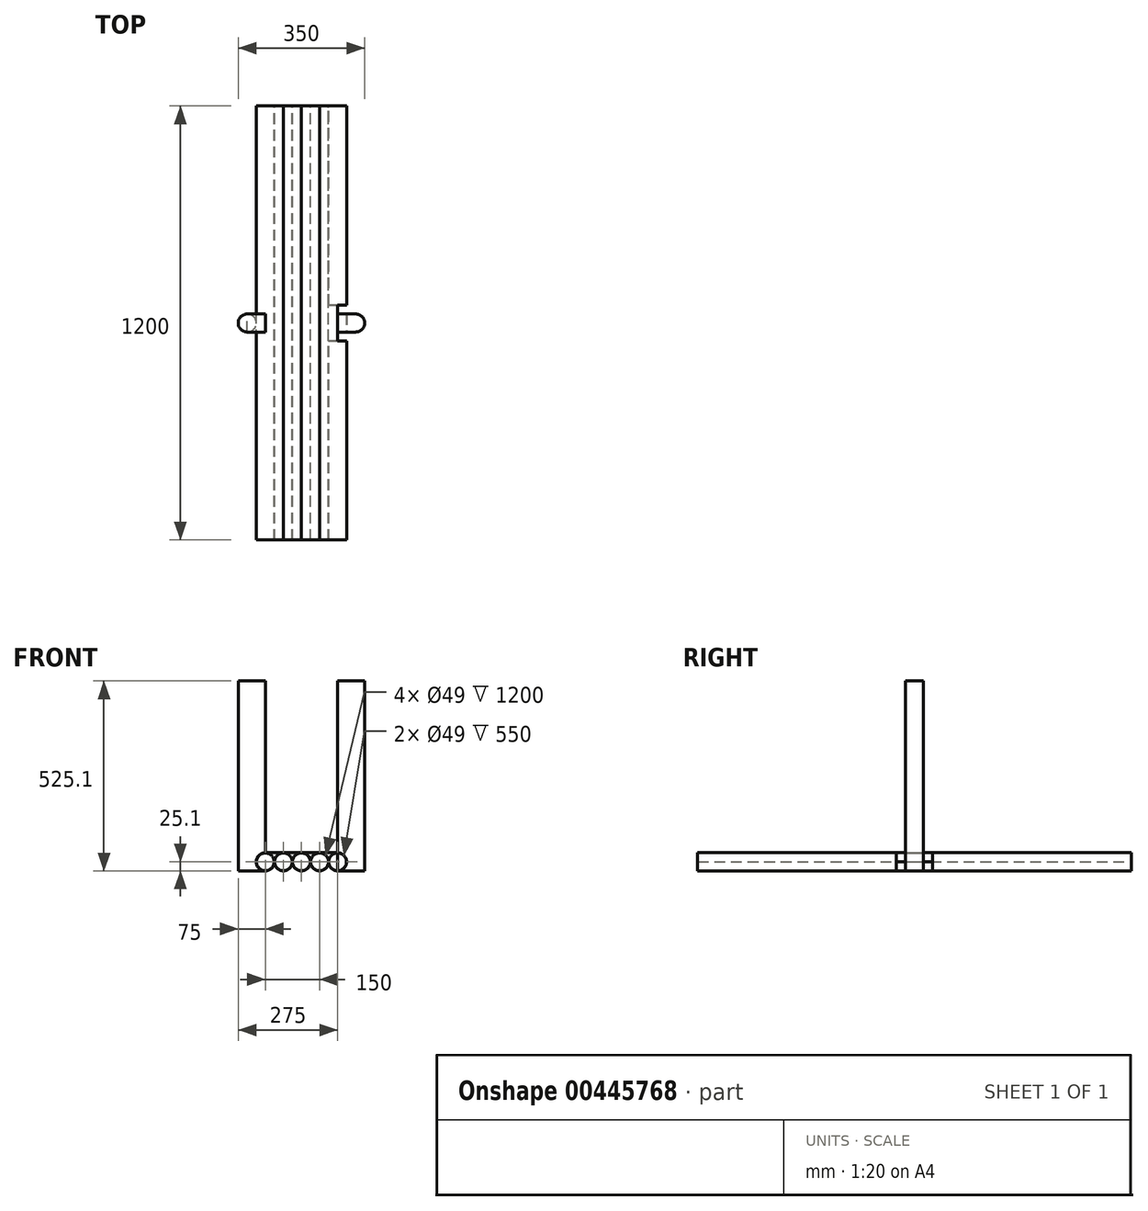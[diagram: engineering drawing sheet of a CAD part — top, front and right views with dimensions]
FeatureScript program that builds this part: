
annotation { "Feature Type Name" : "Feature", "Feature Type Description" : "" }
export const myFeature = defineFeature(function(context is Context, id is Id, definition is map)
    precondition{}
    {
        {
            var Q0;
            Q0=qCreatedBy(makeId("Front.planeOp"),FACE);
            var sketch = newSketch(context, id + "F0", { "sketchPlane" : qUnion([Q0])});
            skCircle(sketch, "E0", {"center": v(0, 0) * mm, "radius": 25 * mm});
            skCircle(sketch, "E1", {"center": v(0, 0) * mm, "radius": 24.5 * mm});
            skCircle(sketch, "E2", {"center": v(-50, 0) * mm, "radius": 25 * mm});
            skCircle(sketch, "E3.MirrorC", {"center": v(-50, 0) * mm, "radius": 24.5 * mm});
            skCircle(sketch, "E4.MirrorC", {"center": v(50, 0) * mm, "radius": 25 * mm});
            skCircle(sketch, "E5.MirrorC", {"center": v(50, 0) * mm, "radius": 24.5 * mm});
            skCircle(sketch, "E6.MirrorC", {"center": v(100, 0) * mm, "radius": 25 * mm});
            skCircle(sketch, "E7.MirrorC", {"center": v(100, 0) * mm, "radius": 24.5 * mm});
            skCircle(sketch, "E8.MirrorC", {"center": v(-100, 0) * mm, "radius": 25 * mm});
            skCircle(sketch, "E9.MirrorC", {"center": v(-100, 0) * mm, "radius": 24.5 * mm});
            skSolve(sketch);
        }
        {
            var Q0;
            Q0=qCreatedBy(makeId("Front.planeOp"),FACE);
            var sketch = newSketch(context, id + "F1", { "sketchPlane" : qUnion([Q0])});
            skCircle(sketch, "E10.0", {"center": v(-100, 0) * mm, "radius": 25 * mm});
            skCircle(sketch, "E11.0", {"center": v(-50, 0) * mm, "radius": 25 * mm});
            skCircle(sketch, "E12.0", {"center": v(0, 0) * mm, "radius": 24.5 * mm});
            skCircle(sketch, "E13.0", {"center": v(50, 0) * mm, "radius": 25 * mm});
            skCircle(sketch, "E14.0", {"center": v(100, 0) * mm, "radius": 25 * mm});
            skCircle(sketch, "E15.0", {"center": v(0, 0) * mm, "radius": 25 * mm});
            skLineSegment(sketch, "E16", {"start": v(-100, 0) * mm, "end": v(-100, 47.4) * mm, "construction": true});
            skLineSegment(sketch, "E17", {"start": v(-100, 25) * mm, "end": v(100, 25) * mm});
            skSolve(sketch);
        }
        {
            var Q0;
            Q0 = qSketchRegion(id + "F0", true);
            extrude(context, id + "F2", {"entities" : qUnion([Q0]), "endBound" : BoundingType.SYMMETRIC, "depth" : 1200 * mm});
        }
        {
            var Q0;
            {var subQ0=sQuery(id+"F1.wireOp",EDGE,"E17");var subQ1=sQuery(id+"F1.wireOp",EDGE,"E13.0");var subQ2=makeQuery(id+"F1.imprint","INTERSECT",VERTEX,{"derivedFrom":[subQ1,subQ0]});Q0=makeQuery(id+"F1.imprint","IMPRINT",FACE,{"disambiguationData":[TD([[makeQuery(id+"F1.imprint","IMPRINT",EDGE,{"disambiguationData":[TD([[subQ2,1.0]])],"derivedFrom":subQ1}),-1.0]])]});}
            var Q1;
            {var subQ0=sQuery(id+"F1.wireOp",EDGE,"E17");var subQ1=sQuery(id+"F1.wireOp",EDGE,"E13.0");var subQ2=makeQuery(id+"F1.imprint","INTERSECT",VERTEX,{"derivedFrom":[subQ1,subQ0]});Q1=makeQuery(id+"F1.imprint","IMPRINT",FACE,{"disambiguationData":[TD([[makeQuery(id+"F1.imprint","IMPRINT",EDGE,{"disambiguationData":[TD([[subQ2,-1.0]])],"derivedFrom":subQ1}),-1.0]])]});}
            var Q2;
            {var subQ0=sQuery(id+"F1.wireOp",EDGE,"E17");var subQ1=sQuery(id+"F1.wireOp",EDGE,"E11.0");var subQ2=makeQuery(id+"F1.imprint","INTERSECT",VERTEX,{"derivedFrom":[subQ1,subQ0]});Q2=makeQuery(id+"F1.imprint","IMPRINT",FACE,{"disambiguationData":[TD([[makeQuery(id+"F1.imprint","IMPRINT",EDGE,{"disambiguationData":[TD([[subQ2,1.0]])],"derivedFrom":subQ1}),-1.0]])]});}
            var Q3;
            {var subQ0=sQuery(id+"F1.wireOp",EDGE,"E17");var subQ1=sQuery(id+"F1.wireOp",EDGE,"E10.0");var subQ2=makeQuery(id+"F1.imprint","INTERSECT",VERTEX,{"derivedFrom":[subQ1,subQ0]});Q3=makeQuery(id+"F1.imprint","IMPRINT",FACE,{"disambiguationData":[TD([[makeQuery(id+"F1.imprint","IMPRINT",EDGE,{"disambiguationData":[TD([[subQ2,1.0]])],"derivedFrom":subQ1}),-1.0]])]});}
            extrude(context, id + "F3", {"entities" : qUnion([Q0, Q1, Q2, Q3]), "endBound" : BoundingType.SYMMETRIC, "depth" : 1200 * mm});
        }
        {
            var Q0;
            Q0=qCreatedBy(makeId("Top.planeOp"),FACE);
            var sketch = newSketch(context, id + "F4", { "sketchPlane" : qUnion([Q0])});
            skCircle(sketch, "E18", {"center": v(-150, 0) * mm, "radius": 25 * mm});
            skLineSegment(sketch, "E19", {"start": v(-75, -600) * mm, "end": v(-75, 600) * mm, "construction": true});
            skLineSegment(sketch, "E20", {"start": v(-150, 0) * mm, "end": v(-150, 25) * mm});
            skLineSegment(sketch, "E21", {"start": v(-150, 25) * mm, "end": v(-150, -25) * mm});
            skLineSegment(sketch, "E22.bottom", {"start": v(-150, -25) * mm, "end": v(-100, -25) * mm});
            skLineSegment(sketch, "E22.top", {"start": v(-150, 25) * mm, "end": v(-100, 25) * mm});
            skLineSegment(sketch, "E22.left", {"start": v(-150, -25) * mm, "end": v(-150, 25) * mm, "construction": true});
            skLineSegment(sketch, "E22.right", {"start": v(-100, -25) * mm, "end": v(-100, 25) * mm});
            skLineSegment(sketch, "E23.MirrorCS", {"start": v(150, -25) * mm, "end": v(100, -25) * mm});
            skLineSegment(sketch, "E24.MirrorCS", {"start": v(150, 25) * mm, "end": v(100, 25) * mm});
            skCircle(sketch, "E25.MirrorC", {"center": v(150, 0) * mm, "radius": 25 * mm});
            skLineSegment(sketch, "E26.MirrorCS", {"start": v(150, -25) * mm, "end": v(150, 25) * mm, "construction": true});
            skLineSegment(sketch, "E27.MirrorCS", {"start": v(100, -25) * mm, "end": v(100, 25) * mm});
            skLineSegment(sketch, "E28.bottom", {"start": v(-150, 25) * mm, "end": v(-125, 25) * mm});
            skLineSegment(sketch, "E28.top", {"start": v(-150, -25) * mm, "end": v(-125, -25) * mm});
            skLineSegment(sketch, "E28.right", {"start": v(-125, 25) * mm, "end": v(-125, -25) * mm});
            skSolve(sketch);
        }
        {
            var Q0;
            Q0 = qSketchRegion(id + "F4", true);
            extrude(context, id + "F5", {"entities" : qUnion([Q0]), "oppositeDirection" : true, "depth" : 25 * mm});
        }
        {
            var Q0;
            Q0 = qSketchRegion(id + "F4", true);
            extrude(context, id + "F6", {"entities" : qUnion([Q0]), "operationType" : NewBodyOperationType.ADD, "depth" : 500 * mm});
        }
        {
            var Q0;
            Q0=makeQuery(id+"F0.imprint","IMPRINT",FACE,{"disambiguationData":[TD([[makeQuery(id+"F0.imprint","IMPRINT",EDGE,{"derivedFrom":sQuery(id+"F0.wireOp",EDGE,"E9.MirrorC")}),1.0]])]});
            extrude(context, id + "F7", {"entities" : qUnion([Q0]), "operationType" : NewBodyOperationType.REMOVE, "endBound" : BoundingType.SYMMETRIC, "oppositeDirection" : true, "depth" : 100 * mm});
        }
        {
            var Q0;
            Q0=makeQuery(id+"F0.imprint","IMPRINT",FACE,{"disambiguationData":[TD([[makeQuery(id+"F0.imprint","IMPRINT",EDGE,{"derivedFrom":sQuery(id+"F0.wireOp",EDGE,"E7.MirrorC")}),-1.0]])]});
            extrude(context, id + "F8", {"entities" : qUnion([Q0]), "operationType" : NewBodyOperationType.REMOVE, "endBound" : BoundingType.SYMMETRIC, "oppositeDirection" : true, "depth" : 100 * mm});
        }
        {
            var Q0;
            {var subQ0=sQuery(id+"F4.wireOp",EDGE,"E22.bottom");Q0=makeQuery(id+"F6.boolean.opBoolean","MERGE",FACE,{"derivedFrom":[makeQuery(id+"F5.opExtrude","SWEPT_FACE",FACE,{"disambiguationData":[OSD([subQ0])]}),makeQuery(id+"F6.opExtrude","SWEPT_FACE",FACE,{"disambiguationData":[OSD([subQ0])]})]});}
            var sketch = newSketch(context, id + "F9", { "sketchPlane" : qUnion([Q0])});
            skCircle(sketch, "E29", {"center": v(-125, 475) * mm, "radius": 25 * mm});
            skSolve(sketch);
        }
        {
            var Q0;
            {var subQ0=sQuery(id+"F9.wireOp",EDGE,"E29");var subQ1=sQuery(id+"F4.wireOp",EDGE,"E22.bottom");var subQ2=makeQuery(id+"F9.imprint","INTERSECT",VERTEX,{"derivedFrom":[makeQuery(id+"F6.opExtrude","CAP_EDGE",EDGE,{"disambiguationData":[OSD([subQ1])],"isStart":false}),subQ0]});Q0=makeQuery(id+"F9.imprint","IMPRINT",FACE,{"disambiguationData":[TD([[makeQuery(id+"F9.imprint","IMPRINT",EDGE,{"disambiguationData":[TD([[subQ2,-1.0]])],"derivedFrom":subQ0}),1.0]])]});}
            extrude(context, id + "F10", {"entities" : qUnion([Q0]), "operationType" : NewBodyOperationType.ADD, "oppositeDirection" : true, "depth" : 25 * mm, "offsetDistance" : 25 * mm});
        }
        {
            var Q0;
            {var subQ0=sQuery(id+"F4.wireOp",EDGE,"E21");var subQ5=makeQuery(id+"F4.imprint","IMPRINT",VERTEX,{"derivedFrom":subQ0});Q0=makeQuery(id+"F4.imprint","IMPRINT",FACE,{"disambiguationData":[TD([[makeQuery(id+"F4.imprint","IMPRINT",EDGE,{"disambiguationData":[TD([[subQ5,1.0]])],"derivedFrom":subQ0}),1.0]])]});}
            var Q1;
            {var subQ0=sQuery(id+"F4.wireOp",EDGE,"E28.bottom");Q1=makeQuery(id+"F4.imprint","IMPRINT",FACE,{"disambiguationData":[TD([[makeQuery(id+"F4.imprint","IMPRINT",EDGE,{"derivedFrom":subQ0}),-1.0]])]});}
            var Q2;
            {var subQ0=sQuery(id+"F4.wireOp",EDGE,"E28.top");Q2=makeQuery(id+"F4.imprint","IMPRINT",FACE,{"disambiguationData":[TD([[makeQuery(id+"F4.imprint","IMPRINT",EDGE,{"derivedFrom":subQ0}),1.0]])]});}
            extrude(context, id + "F11", {"entities" : qUnion([Q0, Q1, Q2]), "operationType" : NewBodyOperationType.ADD, "oppositeDirection" : true, "depth" : 25.1 * mm, "offsetDistance" : 25 * mm});
        }
        {
            var Q0;
            {var subQ0=sQuery(id+"F4.wireOp",EDGE,"E28.top");var subQ1=sQuery(id+"F4.wireOp",EDGE,"E22.bottom");var subQ2=sQuery(id+"F4.wireOp",EDGE,"E28.bottom");var subQ3=sQuery(id+"F4.wireOp",EDGE,"E22.top");var subQ4=sQuery(id+"F4.wireOp",EDGE,"E22.right");Q0=makeQuery(id+"F7.boolean.opBoolean","SPLIT",FACE,{"disambiguationData":[TD([makeQuery(id+"F6.opExtrude","CAP_FACE",FACE,{"disambiguationData":[OSD([sQuery(id+"F4.wireOp",EDGE,"E18"),subQ1,subQ3,subQ4,subQ2,subQ0])],"isStart":false})])],"derivedFrom":makeQuery(id+"F6.boolean.opBoolean","MERGE",FACE,{"derivedFrom":[makeQuery(id+"F5.opExtrude","SWEPT_FACE",FACE,{"disambiguationData":[OSD([subQ4])]}),makeQuery(id+"F6.opExtrude","SWEPT_FACE",FACE,{"disambiguationData":[OSD([subQ4])]})]})});}
            var sketch = newSketch(context, id + "F12", { "sketchPlane" : qUnion([Q0])});
            skCircle(sketch, "E30", {"center": v(0, 475) * mm, "radius": 25 * mm});
            skSolve(sketch);
        }
        {
            var Q0;
            Q0 = qSketchRegion(id + "F12", true);
            extrude(context, id + "F13", {"entities" : qUnion([Q0]), "operationType" : NewBodyOperationType.ADD, "oppositeDirection" : true, "depth" : 25 * mm, "offsetDistance" : 25 * mm});
        }
    });
